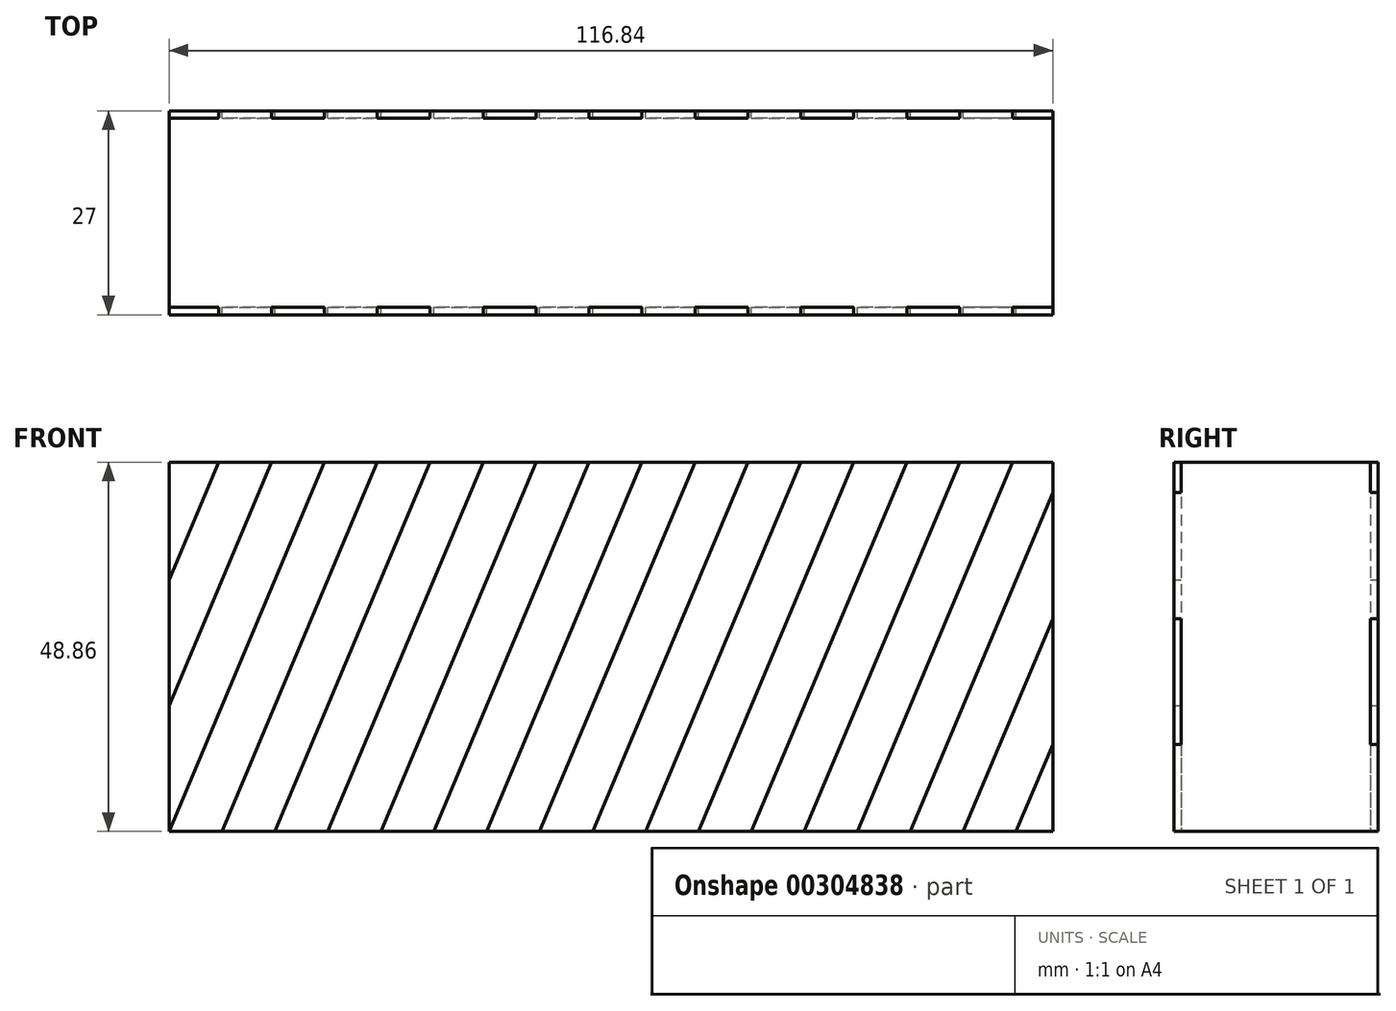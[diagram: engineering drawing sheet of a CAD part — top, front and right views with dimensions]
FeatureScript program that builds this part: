
annotation { "Feature Type Name" : "Feature", "Feature Type Description" : "" }
export const myFeature = defineFeature(function(context is Context, id is Id, definition is map)
    precondition{}
    {
        {
            var Q0;
            Q0=qCreatedBy(makeId("Front.planeOp"),FACE);
            var sketch = newSketch(context, id + "F0", { "sketchPlane" : qUnion([Q0])});
            skLineSegment(sketch, "E0.bottom", {"start": v(31.93, 102.27) * mm, "end": v(148.77, 102.27) * mm});
            skLineSegment(sketch, "E0.top", {"start": v(31.93, 53.4) * mm, "end": v(148.77, 53.4) * mm});
            skLineSegment(sketch, "E0.left", {"start": v(31.93, 102.27) * mm, "end": v(31.93, 53.4) * mm});
            skLineSegment(sketch, "E0.right", {"start": v(148.77, 102.27) * mm, "end": v(148.77, 53.4) * mm});
            skLineSegment(sketch, "E1", {"start": v(31.93, 53.4) * mm, "end": v(52.46, 102.27) * mm});
            skLineSegment(sketch, "E2.1.0.0", {"start": v(38.93, 53.4) * mm, "end": v(59.46, 102.27) * mm});
            skLineSegment(sketch, "E2.2.0.0", {"start": v(45.93, 53.4) * mm, "end": v(66.46, 102.27) * mm});
            skLineSegment(sketch, "E2.3.0.0", {"start": v(52.93, 53.4) * mm, "end": v(73.46, 102.27) * mm});
            skLineSegment(sketch, "E2.4.0.0", {"start": v(59.93, 53.4) * mm, "end": v(80.46, 102.27) * mm});
            skLineSegment(sketch, "E2.5.0.0", {"start": v(66.93, 53.4) * mm, "end": v(87.46, 102.27) * mm});
            skLineSegment(sketch, "E2.6.0.0", {"start": v(73.93, 53.4) * mm, "end": v(94.46, 102.27) * mm});
            skLineSegment(sketch, "E2.7.0.0", {"start": v(80.93, 53.4) * mm, "end": v(101.46, 102.27) * mm});
            skLineSegment(sketch, "E2.8.0.0", {"start": v(87.93, 53.4) * mm, "end": v(108.46, 102.27) * mm});
            skLineSegment(sketch, "E2.9.0.0", {"start": v(94.93, 53.4) * mm, "end": v(115.46, 102.27) * mm});
            skLineSegment(sketch, "E2.10.0.0", {"start": v(101.93, 53.4) * mm, "end": v(122.46, 102.27) * mm});
            skLineSegment(sketch, "E2.11.0.0", {"start": v(108.93, 53.4) * mm, "end": v(129.46, 102.27) * mm});
            skLineSegment(sketch, "E2.12.0.0", {"start": v(115.93, 53.4) * mm, "end": v(136.46, 102.27) * mm});
            skLineSegment(sketch, "E2.13.0.0", {"start": v(122.93, 53.4) * mm, "end": v(143.46, 102.27) * mm});
            skLineSegment(sketch, "E2.14.0.0", {"start": v(129.93, 53.4) * mm, "end": v(148.77, 98.24) * mm});
            skLineSegment(sketch, "E2.15.0.0", {"start": v(136.93, 53.4) * mm, "end": v(148.77, 81.58) * mm});
            skLineSegment(sketch, "E2.16.0.0", {"start": v(143.93, 53.4) * mm, "end": v(148.77, 64.93) * mm});
            skLineSegment(sketch, "E2.direction1", {"start": v(31.93, 53.4) * mm, "end": v(38.93, 53.4) * mm, "construction": true});
            skPoint(sketch, "E3.orphan", {"position": v(164.46, 102.27) * mm});
            skPoint(sketch, "E4.orphan", {"position": v(157.46, 102.27) * mm});
            skLineSegment(sketch, "E5.1.0.0", {"start": v(31.93, 70.06) * mm, "end": v(45.46, 102.27) * mm});
            skLineSegment(sketch, "E5.2.0.0", {"start": v(31.93, 86.72) * mm, "end": v(38.46, 102.27) * mm});
            skLineSegment(sketch, "E5.direction1", {"start": v(31.93, 53.4) * mm, "end": v(24.93, 53.4) * mm, "construction": true});
            skPoint(sketch, "E6.orphan", {"position": v(17.93, 53.4) * mm});
            skPoint(sketch, "E7.orphan", {"position": v(150.46, 102.27) * mm});
            skSolve(sketch);
        }
        {
            var Q0;
            {var subQ0=sQuery(id+"F0.wireOp",EDGE,"E2.14.0.0");Q0=makeQuery(id+"F0.imprint","IMPRINT",FACE,{"disambiguationData":[TD([[makeQuery(id+"F0.imprint","IMPRINT",EDGE,{"derivedFrom":subQ0}),-1.0]])]});}
            var Q1;
            {var subQ0=sQuery(id+"F0.wireOp",EDGE,"E2.11.0.0");Q1=makeQuery(id+"F0.imprint","IMPRINT",FACE,{"disambiguationData":[TD([[makeQuery(id+"F0.imprint","IMPRINT",EDGE,{"derivedFrom":subQ0}),-1.0]])]});}
            var Q2;
            {var subQ0=sQuery(id+"F0.wireOp",EDGE,"E2.13.0.0");Q2=makeQuery(id+"F0.imprint","IMPRINT",FACE,{"disambiguationData":[TD([[makeQuery(id+"F0.imprint","IMPRINT",EDGE,{"derivedFrom":subQ0}),-1.0]])]});}
            var Q3;
            {var subQ0=sQuery(id+"F0.wireOp",EDGE,"E2.8.0.0");Q3=makeQuery(id+"F0.imprint","IMPRINT",FACE,{"disambiguationData":[TD([[makeQuery(id+"F0.imprint","IMPRINT",EDGE,{"derivedFrom":subQ0}),-1.0]])]});}
            var Q4;
            {var subQ0=sQuery(id+"F0.wireOp",EDGE,"E2.7.0.0");Q4=makeQuery(id+"F0.imprint","IMPRINT",FACE,{"disambiguationData":[TD([[makeQuery(id+"F0.imprint","IMPRINT",EDGE,{"derivedFrom":subQ0}),-1.0]])]});}
            var Q5;
            {var subQ0=sQuery(id+"F0.wireOp",EDGE,"E2.6.0.0");Q5=makeQuery(id+"F0.imprint","IMPRINT",FACE,{"disambiguationData":[TD([[makeQuery(id+"F0.imprint","IMPRINT",EDGE,{"derivedFrom":subQ0}),-1.0]])]});}
            var Q6;
            {var subQ0=sQuery(id+"F0.wireOp",EDGE,"E2.5.0.0");Q6=makeQuery(id+"F0.imprint","IMPRINT",FACE,{"disambiguationData":[TD([[makeQuery(id+"F0.imprint","IMPRINT",EDGE,{"derivedFrom":subQ0}),-1.0]])]});}
            var Q7;
            {var subQ0=sQuery(id+"F0.wireOp",EDGE,"E2.4.0.0");Q7=makeQuery(id+"F0.imprint","IMPRINT",FACE,{"disambiguationData":[TD([[makeQuery(id+"F0.imprint","IMPRINT",EDGE,{"derivedFrom":subQ0}),-1.0]])]});}
            var Q8;
            {var subQ0=sQuery(id+"F0.wireOp",EDGE,"E2.3.0.0");Q8=makeQuery(id+"F0.imprint","IMPRINT",FACE,{"disambiguationData":[TD([[makeQuery(id+"F0.imprint","IMPRINT",EDGE,{"derivedFrom":subQ0}),-1.0]])]});}
            var Q9;
            {var subQ0=sQuery(id+"F0.wireOp",EDGE,"E2.2.0.0");Q9=makeQuery(id+"F0.imprint","IMPRINT",FACE,{"disambiguationData":[TD([[makeQuery(id+"F0.imprint","IMPRINT",EDGE,{"derivedFrom":subQ0}),-1.0]])]});}
            var Q10;
            {var subQ0=sQuery(id+"F0.wireOp",EDGE,"E2.1.0.0");Q10=makeQuery(id+"F0.imprint","IMPRINT",FACE,{"disambiguationData":[TD([[makeQuery(id+"F0.imprint","IMPRINT",EDGE,{"derivedFrom":subQ0}),-1.0]])]});}
            var Q11;
            {var subQ0=sQuery(id+"F0.wireOp",EDGE,"E1");Q11=makeQuery(id+"F0.imprint","IMPRINT",FACE,{"disambiguationData":[TD([[makeQuery(id+"F0.imprint","IMPRINT",EDGE,{"derivedFrom":subQ0}),-1.0]])]});}
            var Q12;
            {var subQ0=sQuery(id+"F0.wireOp",EDGE,"E1");Q12=makeQuery(id+"F0.imprint","IMPRINT",FACE,{"disambiguationData":[TD([[makeQuery(id+"F0.imprint","IMPRINT",EDGE,{"derivedFrom":subQ0}),1.0]])]});}
            var Q13;
            {var subQ0=sQuery(id+"F0.wireOp",EDGE,"E5.1.0.0");Q13=makeQuery(id+"F0.imprint","IMPRINT",FACE,{"disambiguationData":[TD([[makeQuery(id+"F0.imprint","IMPRINT",EDGE,{"derivedFrom":subQ0}),1.0]])]});}
            var Q14;
            {var subQ3=sQuery(id+"F0.wireOp",EDGE,"E2.16.0.0");Q14=makeQuery(id+"F0.imprint","IMPRINT",FACE,{"disambiguationData":[TD([[makeQuery(id+"F0.imprint","IMPRINT",EDGE,{"derivedFrom":subQ3}),-1.0]])]});}
            var Q15;
            {var subQ3=sQuery(id+"F0.wireOp",EDGE,"E5.2.0.0");Q15=makeQuery(id+"F0.imprint","IMPRINT",FACE,{"disambiguationData":[TD([[makeQuery(id+"F0.imprint","IMPRINT",EDGE,{"derivedFrom":subQ3}),1.0]])]});}
            var Q16;
            {var subQ0=sQuery(id+"F0.wireOp",EDGE,"E2.12.0.0");Q16=makeQuery(id+"F0.imprint","IMPRINT",FACE,{"disambiguationData":[TD([[makeQuery(id+"F0.imprint","IMPRINT",EDGE,{"derivedFrom":subQ0}),-1.0]])]});}
            var Q17;
            {var subQ0=sQuery(id+"F0.wireOp",EDGE,"E2.10.0.0");Q17=makeQuery(id+"F0.imprint","IMPRINT",FACE,{"disambiguationData":[TD([[makeQuery(id+"F0.imprint","IMPRINT",EDGE,{"derivedFrom":subQ0}),-1.0]])]});}
            var Q18;
            {var subQ0=sQuery(id+"F0.wireOp",EDGE,"E2.9.0.0");Q18=makeQuery(id+"F0.imprint","IMPRINT",FACE,{"disambiguationData":[TD([[makeQuery(id+"F0.imprint","IMPRINT",EDGE,{"derivedFrom":subQ0}),-1.0]])]});}
            var Q19;
            {var subQ0=sQuery(id+"F0.wireOp",EDGE,"E2.15.0.0");Q19=makeQuery(id+"F0.imprint","IMPRINT",FACE,{"disambiguationData":[TD([[makeQuery(id+"F0.imprint","IMPRINT",EDGE,{"derivedFrom":subQ0}),-1.0]])]});}
            extrude(context, id + "F1", {"entities" : qUnion([Q0, Q1, Q2, Q3, Q4, Q5, Q6, Q7, Q8, Q9, Q10, Q11, Q12, Q13, Q14, Q15, Q16, Q17, Q18, Q19]), "oppositeDirection" : true, "depth" : 25 * mm});
        }
        {
            var Q0;
            {var subQ0=sQuery(id+"F0.wireOp",EDGE,"E5.1.0.0");Q0=makeQuery(id+"F0.imprint","IMPRINT",FACE,{"disambiguationData":[TD([[makeQuery(id+"F0.imprint","IMPRINT",EDGE,{"derivedFrom":subQ0}),1.0]])]});}
            var Q1;
            {var subQ0=sQuery(id+"F0.wireOp",EDGE,"E1");Q1=makeQuery(id+"F0.imprint","IMPRINT",FACE,{"disambiguationData":[TD([[makeQuery(id+"F0.imprint","IMPRINT",EDGE,{"derivedFrom":subQ0}),-1.0]])]});}
            var Q2;
            {var subQ0=sQuery(id+"F0.wireOp",EDGE,"E2.2.0.0");Q2=makeQuery(id+"F0.imprint","IMPRINT",FACE,{"disambiguationData":[TD([[makeQuery(id+"F0.imprint","IMPRINT",EDGE,{"derivedFrom":subQ0}),-1.0]])]});}
            var Q3;
            {var subQ0=sQuery(id+"F0.wireOp",EDGE,"E2.4.0.0");Q3=makeQuery(id+"F0.imprint","IMPRINT",FACE,{"disambiguationData":[TD([[makeQuery(id+"F0.imprint","IMPRINT",EDGE,{"derivedFrom":subQ0}),-1.0]])]});}
            var Q4;
            {var subQ0=sQuery(id+"F0.wireOp",EDGE,"E2.6.0.0");Q4=makeQuery(id+"F0.imprint","IMPRINT",FACE,{"disambiguationData":[TD([[makeQuery(id+"F0.imprint","IMPRINT",EDGE,{"derivedFrom":subQ0}),-1.0]])]});}
            var Q5;
            {var subQ0=sQuery(id+"F0.wireOp",EDGE,"E2.8.0.0");Q5=makeQuery(id+"F0.imprint","IMPRINT",FACE,{"disambiguationData":[TD([[makeQuery(id+"F0.imprint","IMPRINT",EDGE,{"derivedFrom":subQ0}),-1.0]])]});}
            var Q6;
            {var subQ0=sQuery(id+"F0.wireOp",EDGE,"E2.10.0.0");Q6=makeQuery(id+"F0.imprint","IMPRINT",FACE,{"disambiguationData":[TD([[makeQuery(id+"F0.imprint","IMPRINT",EDGE,{"derivedFrom":subQ0}),-1.0]])]});}
            var Q7;
            {var subQ0=sQuery(id+"F0.wireOp",EDGE,"E2.12.0.0");Q7=makeQuery(id+"F0.imprint","IMPRINT",FACE,{"disambiguationData":[TD([[makeQuery(id+"F0.imprint","IMPRINT",EDGE,{"derivedFrom":subQ0}),-1.0]])]});}
            var Q8;
            {var subQ0=sQuery(id+"F0.wireOp",EDGE,"E2.14.0.0");Q8=makeQuery(id+"F0.imprint","IMPRINT",FACE,{"disambiguationData":[TD([[makeQuery(id+"F0.imprint","IMPRINT",EDGE,{"derivedFrom":subQ0}),-1.0]])]});}
            var Q9;
            {var subQ3=sQuery(id+"F0.wireOp",EDGE,"E2.16.0.0");Q9=makeQuery(id+"F0.imprint","IMPRINT",FACE,{"disambiguationData":[TD([[makeQuery(id+"F0.imprint","IMPRINT",EDGE,{"derivedFrom":subQ3}),-1.0]])]});}
            extrude(context, id + "F2", {"entities" : qUnion([Q0, Q1, Q2, Q3, Q4, Q5, Q6, Q7, Q8, Q9]), "operationType" : NewBodyOperationType.ADD, "depth" : 1 * mm, "hasSecondDirection" : true, "secondDirectionOppositeDirection" : true, "secondDirectionDepth" : 26 * mm});
        }
    });
